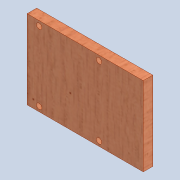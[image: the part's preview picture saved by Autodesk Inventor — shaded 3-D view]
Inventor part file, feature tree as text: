
AUTODESK INVENTOR PART (.ipt)
format: ipt  version: 2020 (Build 240168000, 168)  size: 123,904 bytes
history: native  units: mm
features: sketch x2, extrude x1, hole x1, pattern_linear x1
ambient origin geometry x8: Origin, YZ Plane, XZ Plane, XY Plane, X Axis, Y Axis, Z Axis, Center Point
bodies: Solid1 (feature_tree)
feature tree (5):
  extrude  "Extrusion1"  Depth=66.0mm
  hole  "Hole1"  [1 undecoded]
  pattern_linear  "Rectangular Pattern1"  Spacing1=4.0mm  [1 undecoded]
  sketch  "Sketch1"  dims[d0=97.0mm d1=66.0mm]
  sketch  "Sketch4"  dims[d2=8.0mm d3=0.0mm d19=10.0mm d20=4.0mm d21=4.0mm d22=4.5mm d23=6.0mm d24=4.0mm d25=2.0mm d26=90.0deg d27=8.0mm d28=20.594885mm d29=20.0mm d31=50.0mm]
note: 2 required parameter values undecoded (feature->parameter linkage not recoverable at this tier; creation-order binding heuristic only, values carry confidence <= 0.55)
